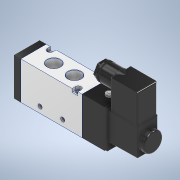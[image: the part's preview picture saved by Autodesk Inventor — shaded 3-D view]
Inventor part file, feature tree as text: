
AUTODESK INVENTOR PART (.ipt)
format: ipt  version: 2020 (Build 240168000, 168)  size: 348,672 bytes
history: native  units: in
note: dims shown in document units (in); Inventor stores cm internally (conversion verified against a paired STEP export)
features: fillet x4
ambient origin geometry x8: Origin, YZ Plane, XZ Plane, XY Plane, X Axis, Y Axis, Z Axis, Center Point
bodies: Solid1 (feature_tree), Solid2 (feature_tree), Solid3 (feature_tree), Solid4 (feature_tree)
feature tree (4):
  fillet  "Fillet6"  [1 undecoded]
  fillet  "Fillet5"  [1 undecoded]
  fillet  "Fillet10"  [1 undecoded]
  fillet  "Fillet11"  [1 undecoded]
note: 4 required parameter values undecoded (feature->parameter linkage not recoverable at this tier; creation-order binding heuristic only, values carry confidence <= 0.55)
